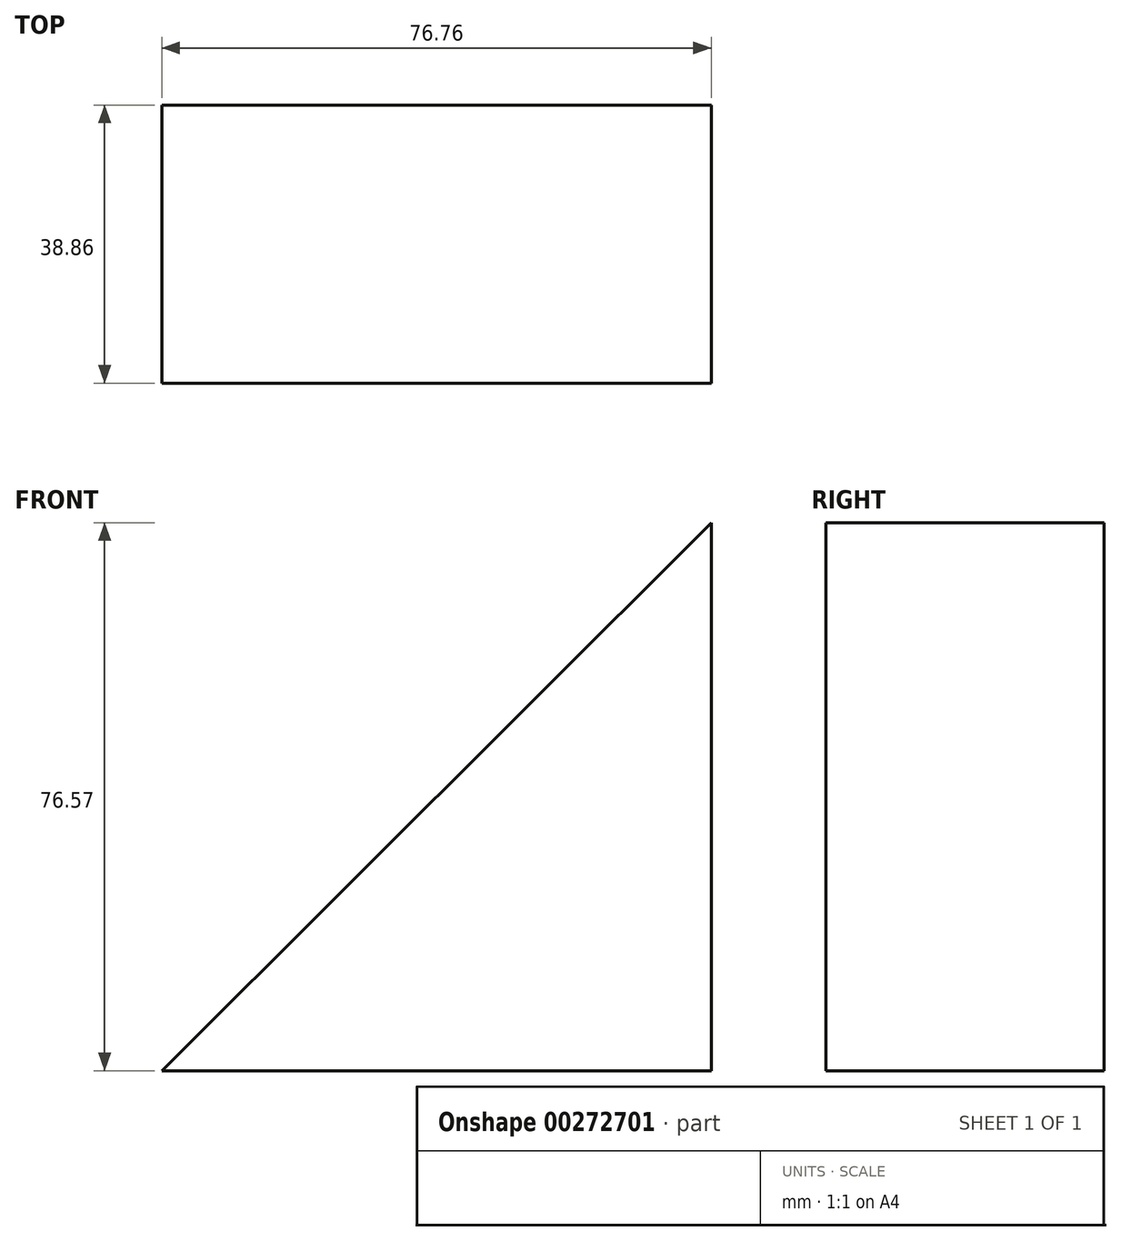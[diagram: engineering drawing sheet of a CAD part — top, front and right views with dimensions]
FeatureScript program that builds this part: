
annotation { "Feature Type Name" : "Feature", "Feature Type Description" : "" }
export const myFeature = defineFeature(function(context is Context, id is Id, definition is map)
    precondition{}
    {
        {
            var Q0;
            Q0=qCreatedBy(makeId("Front.planeOp"),FACE);
            var sketch = newSketch(context, id + "F0", { "sketchPlane" : qUnion([Q0])});
            skLineSegment(sketch, "E0", {"start": v(0, 0) * mm, "end": v(-76.76, 0) * mm});
            skLineSegment(sketch, "E1", {"start": v(-76.76, 0) * mm, "end": v(0, 76.57) * mm});
            skLineSegment(sketch, "E2", {"start": v(0, 76.57) * mm, "end": v(0, 0) * mm});
            skSolve(sketch);
        }
        {
            var Q0;
            Q0 = qSketchRegion(id + "F0", true);
            extrude(context, id + "F1", {"entities" : qUnion([Q0]), "depth" : 38.86 * mm});
        }
    });
